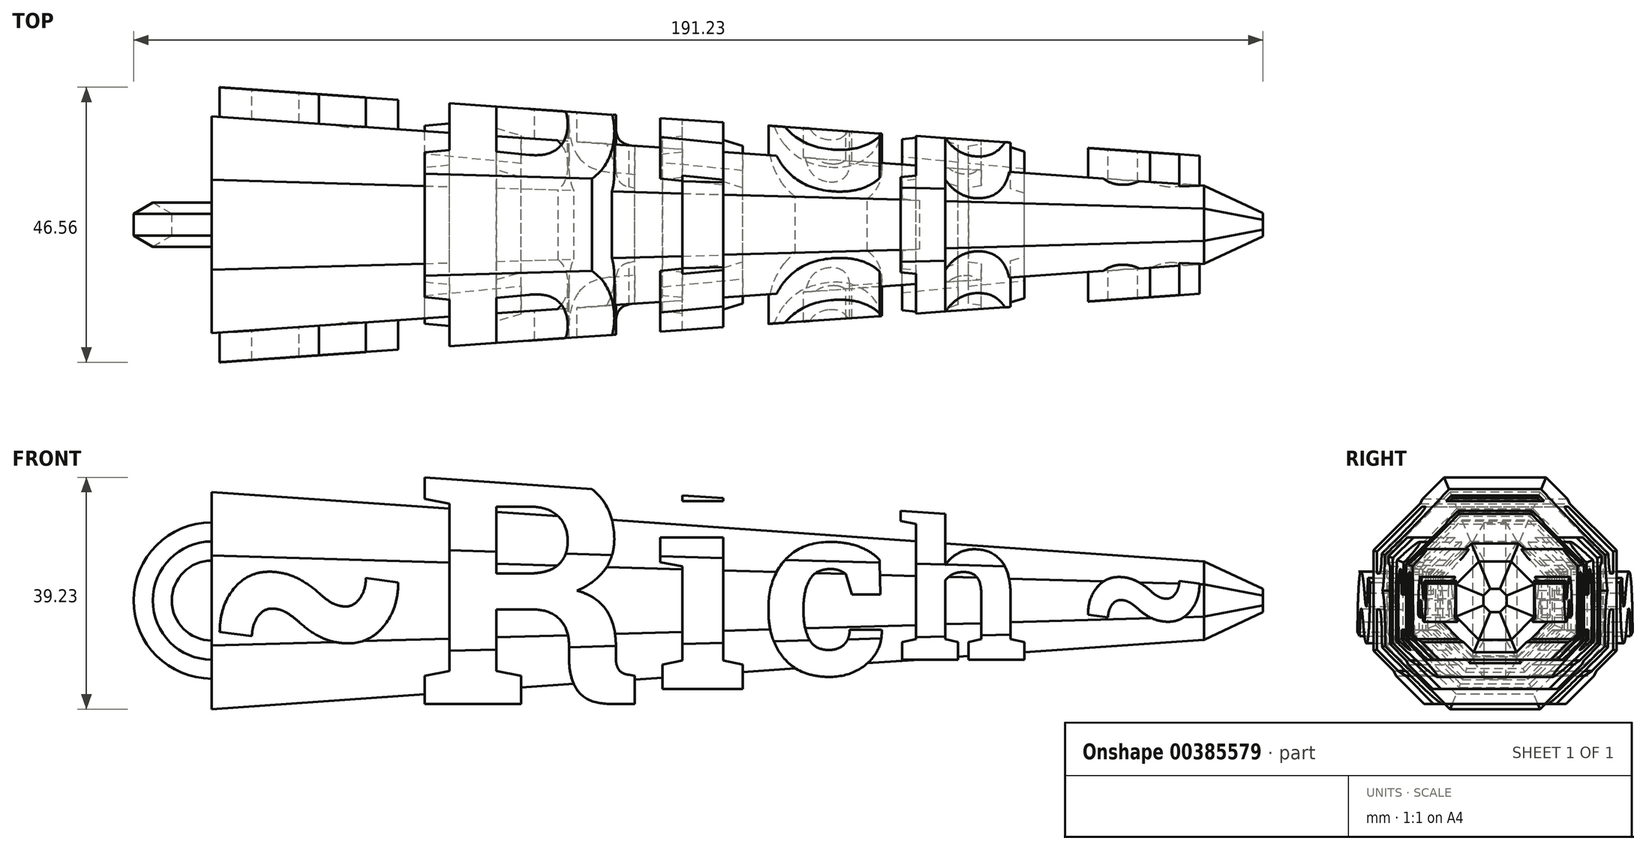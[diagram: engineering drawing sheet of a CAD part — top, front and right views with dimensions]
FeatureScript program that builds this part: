
annotation { "Feature Type Name" : "Feature", "Feature Type Description" : "" }
export const myFeature = defineFeature(function(context is Context, id is Id, definition is map)
    precondition{}
    {
        {
            assignVariable(context, id + "F0", {"name" : "hookPlane", "anyValue" : 84});
        }
        {
            assignVariable(context, id + "F1", {"name" : "halfLength", "anyValue" : 84});
        }
        {
            var Q0;
            Q0=qCreatedBy(makeId("Front.planeOp"),FACE);
            var sketch = newSketch(context, id + "F2", { "sketchPlane" : qUnion([Q0])});
            skText(sketch, "E0", { "text": "~R", "fontName": "RobotoSlab-Bold.ttf"});
            skPoint(sketch, "E1", {"position": v(-8.97, 0) * mm});
            skText(sketch, "E2", { "text": "i", "fontName": "RobotoSlab-Bold.ttf"});
            skText(sketch, "E3", { "text": "c", "fontName": "RobotoSlab-Bold.ttf"});
            skText(sketch, "E4", { "text": "h ~", "fontName": "RobotoSlab-Bold.ttf"});
            skPoint(sketch, "E5", {"position": v(8.89, 0) * mm});
            skPoint(sketch, "E6", {"position": v(32.07, 0) * mm});
            skLineSegment(sketch, "E7", {"start": v(-85.37, -20) * mm, "end": v(-85.37, -51.65) * mm, "construction": true});
            skLineSegment(sketch, "E8", {"start": v(-85.37, -51.65) * mm, "end": v(85.37, -51.65) * mm, "construction": true});
            skLineSegment(sketch, "E9", {"start": v(85.37, -51.65) * mm, "end": v(85.37, -12.5) * mm, "construction": true});
            skPoint(sketch, "E10", {"position": v(0, -51.65) * mm});
            const initialGuessF2  = {"E0": [-0.08537, -0.02, 1, 0, 0.04], "E2": [-0.00897, -0.0175, 1, 0, 0.035], "E3": [0.00889, -0.015, 1, 0, 0.03], "E4": [0.03207, -0.0125, 1, 0, 0.025]};
            skSetInitialGuess(sketch, initialGuessF2);
            skSolve(sketch);
        }
        {
            var Q0;
            Q0=qSketchRegion(id+"F2",true);
            extrude(context, id + "F3", {"entities" : qUnion([Q0]), "depth" : 25 * mm, "hasSecondDirection" : true, "secondDirectionOppositeDirection" : true, "secondDirectionDepth" : 25 * mm});
        }
        {
            var Q0;
            Q0=qCreatedBy(makeId("Right.planeOp"),FACE);
            var sketch = newSketch(context, id + "F4", { "sketchPlane" : qUnion([Q0])});
            skCircle(sketch, "E11", {"center": v(0, -2.5) * mm, "radius": 12.5 * mm, "construction": true});
            skLineSegment(sketch, "E12", {"start": v(0, 19.5) * mm, "end": v(0, 14.75) * mm, "construction": true});
            skLineSegment(sketch, "E13.0", {"start": v(-5.18, 10) * mm, "end": v(5.18, 10) * mm});
            skLineSegment(sketch, "E13.1", {"start": v(5.18, 10) * mm, "end": v(12.5, 2.67) * mm});
            skLineSegment(sketch, "E13.2", {"start": v(12.5, 2.67) * mm, "end": v(12.5, -7.68) * mm});
            skLineSegment(sketch, "E13.3", {"start": v(12.5, -7.68) * mm, "end": v(5.18, -15) * mm});
            skLineSegment(sketch, "E13.4", {"start": v(5.18, -15) * mm, "end": v(-5.18, -15) * mm});
            skLineSegment(sketch, "E13.5", {"start": v(-5.18, -15) * mm, "end": v(-12.5, -7.68) * mm});
            skLineSegment(sketch, "E13.6", {"start": v(-12.5, -7.68) * mm, "end": v(-12.5, 2.67) * mm});
            skLineSegment(sketch, "E13.7", {"start": v(-12.5, 2.67) * mm, "end": v(-5.18, 10) * mm});
            skPoint(sketch, "E13.0.midPoint", {"position": v(0, 10) * mm});
            skLineSegment(sketch, "E14", {"start": v(0, 19.5) * mm, "end": v(0, 10) * mm});
            skSolve(sketch);
        }
        {
            var Q0;
            Q0=qSketchRegion(id+"F4",true);
            var Q1;
            Q1=makeQuery(id+"F3.opExtrude","SWEPT_FACE",FACE,{"disambiguationData":[OSD([sQuery(id+"F2.wireOp",EDGE,"E4.sketch_text.stroke-1")])]});
            extrude(context, id + "F5", {"entities" : qUnion([Q0]), "operationType" : NewBodyOperationType.ADD, "oppositeDirection" : true, "depth" : (getVariable(context, 'halfLength')) * mm, "hasDraft" : true, "draftAngle" : 4 * degree, "hasSecondDirection" : true, "secondDirectionOppositeDirection" : false, "secondDirectionBoundEntityFace" : qUnion([Q1]), "secondDirectionDepth" : (getVariable(context, 'halfLength')) * mm, "hasSecondDirectionDraft" : true, "secondDirectionDraftAngle" : 4 * degree, "secondDirectionDraftPullDirection" : true});
        }
        {
            var Q0;
            Q0=qCreatedBy(makeId("Right.planeOp"),FACE);
            var sketch = newSketch(context, id + "F6", { "sketchPlane" : qUnion([Q0])});
            skCircle(sketch, "E15.cCircle", {"center": v(0, -2.5) * mm, "radius": 17.5 * mm, "construction": true});
            skLineSegment(sketch, "E15.0", {"start": v(-7.25, 15) * mm, "end": v(7.25, 15) * mm});
            skLineSegment(sketch, "E15.1", {"start": v(7.25, 15) * mm, "end": v(17.5, 4.75) * mm});
            skLineSegment(sketch, "E15.2", {"start": v(17.5, 4.75) * mm, "end": v(17.5, -9.75) * mm});
            skLineSegment(sketch, "E15.3", {"start": v(17.5, -9.75) * mm, "end": v(7.25, -20) * mm});
            skLineSegment(sketch, "E15.4", {"start": v(7.25, -20) * mm, "end": v(-7.25, -20) * mm});
            skLineSegment(sketch, "E15.5", {"start": v(-7.25, -20) * mm, "end": v(-17.5, -9.75) * mm});
            skLineSegment(sketch, "E15.6", {"start": v(-17.5, -9.75) * mm, "end": v(-17.5, 4.75) * mm});
            skLineSegment(sketch, "E15.7", {"start": v(-17.5, 4.75) * mm, "end": v(-7.25, 15) * mm});
            skLineSegment(sketch, "E16.bottom", {"start": v(37.5, 35) * mm, "end": v(-37.5, 35) * mm});
            skLineSegment(sketch, "E16.top", {"start": v(37.5, -40) * mm, "end": v(-37.5, -40) * mm});
            skLineSegment(sketch, "E16.left", {"start": v(37.5, 35) * mm, "end": v(37.5, -40) * mm});
            skLineSegment(sketch, "E16.right", {"start": v(-37.5, 35) * mm, "end": v(-37.5, -40) * mm});
            skLineSegment(sketch, "E17", {"start": v(0, 19.5) * mm, "end": v(0, -8.52) * mm, "construction": true});
            skSolve(sketch);
        }
        {
            var Q0;
            Q0=makeQuery(id+"F6.imprint","IMPRINT",FACE,{"disambiguationData":[TD([[makeQuery(id+"F6.imprint","IMPRINT",EDGE,{"derivedFrom":sQuery(id+"F6.wireOp",EDGE,"E15.0")}),1.0]])]});
            extrude(context, id + "F7", {"entities" : qUnion([Q0]), "operationType" : NewBodyOperationType.REMOVE, "endBound" : BoundingType.THROUGH_ALL, "depth" : 25 * mm, "hasDraft" : true, "draftAngle" : 4 * degree, "hasSecondDirection" : true, "secondDirectionBound" : SecondDirectionBoundingType.THROUGH_ALL, "secondDirectionOppositeDirection" : true, "secondDirectionDepth" : 25 * mm, "hasSecondDirectionDraft" : true, "secondDirectionDraftAngle" : 4 * degree, "secondDirectionDraftPullDirection" : true});
        }
        {
            var Q0;
            {var subQ0=sQuery(id+"F4.wireOp",EDGE,"E13.3");var subQ1=sQuery(id+"F4.wireOp",EDGE,"E13.2");var subQ2=sQuery(id+"F4.wireOp",EDGE,"E13.4");var subQ3=sQuery(id+"F4.wireOp",EDGE,"E13.5");var subQ4=sQuery(id+"F4.wireOp",EDGE,"E13.6");Q0=makeQuery(id+"F5.boolean.opBoolean","SPLIT",FACE,{"disambiguationData":[TD([makeQuery(id+"F3.opExtrude","SWEPT_FACE",FACE,{"disambiguationData":[OSD([sQuery(id+"F2.wireOp",EDGE,"E4.sketch_text.stroke-0")])]})])],"derivedFrom":makeQuery(id+"F5.opExtrude","CAP_FACE",FACE,{"disambiguationData":[OSD([sQuery(id+"F4.wireOp",EDGE,"E13.0"),sQuery(id+"F4.wireOp",EDGE,"E13.1"),subQ1,subQ0,subQ2,subQ3,subQ4,sQuery(id+"F4.wireOp",EDGE,"E13.7")])],"isStart":true})});}
            var sketch = newSketch(context, id + "F8", { "sketchPlane" : qUnion([Q0])});
            skCircle(sketch, "E18.cCircle", {"center": v(0, -2.5) * mm, "radius": 6.63 * mm, "construction": true});
            skLineSegment(sketch, "E18.0", {"start": v(-2.74, 4.12) * mm, "end": v(2.74, 4.12) * mm});
            skLineSegment(sketch, "E18.1", {"start": v(2.74, 4.12) * mm, "end": v(6.63, 0.24) * mm});
            skLineSegment(sketch, "E18.2", {"start": v(6.63, 0.24) * mm, "end": v(6.63, -5.25) * mm});
            skLineSegment(sketch, "E18.3", {"start": v(6.63, -5.25) * mm, "end": v(2.74, -9.13) * mm});
            skLineSegment(sketch, "E18.4", {"start": v(2.74, -9.13) * mm, "end": v(-2.74, -9.13) * mm});
            skLineSegment(sketch, "E18.5", {"start": v(-2.74, -9.13) * mm, "end": v(-6.63, -5.25) * mm});
            skLineSegment(sketch, "E18.6", {"start": v(-6.63, -5.25) * mm, "end": v(-6.63, 0.24) * mm});
            skLineSegment(sketch, "E18.7", {"start": v(-6.63, 0.24) * mm, "end": v(-2.74, 4.12) * mm});
            skPoint(sketch, "E18.0.midPoint", {"position": v(0, 4.12) * mm});
            skLineSegment(sketch, "E19", {"start": v(0, 19.59) * mm, "end": v(0, -20.57) * mm, "construction": true});
            skSolve(sketch);
        }
        {
            var Q0;
            Q0=qSketchRegion(id+"F8",true);
            extrude(context, id + "F9", {"entities" : qUnion([Q0]), "operationType" : NewBodyOperationType.ADD, "depth" : 10 * mm, "hasDraft" : true, "draftAngle" : 25 * degree, "draftPullDirection" : true});
        }
        {
            var Q0;
            Q0=qCreatedBy(makeId("Right.planeOp"),FACE);
            cPlane(context, id + "F10", {"entities" : qUnion([Q0]), "cplaneType" : CPlaneType.OFFSET, "offset" : (getVariable(context, 'hookPlane')) * mm, "oppositeDirection" : true, "width" : 150 * mm, "height" : 150 * mm});
        }
        {
            var Q0;
            Q0=qCreatedBy(makeId("Front.planeOp"),FACE);
            var sketch = newSketch(context, id + "F11", { "sketchPlane" : qUnion([Q0])});
            skArc(sketch, "E20", {"start": v(-77.39, 5) * mm, "mid": v(-94, -2.5) * mm, "end": v(-77.39, -10) * mm});
            skLineSegment(sketch, "E21", {"start": v(-77.39, 5) * mm, "end": v(-77.39, -10) * mm, "construction": true});
            skPoint(sketch, "E22", {"position": v(-77.39, -2.5) * mm});
            skLineSegment(sketch, "E23", {"start": v(-84, 15.87) * mm, "end": v(-84, -20.88) * mm, "construction": true});
            skSolve(sketch);
        }
        {
            var Q0;
            Q0=qCreatedBy(id+"F10.planeOp",FACE);
            var sketch = newSketch(context, id + "F12", { "sketchPlane" : qUnion([Q0])});
            skCircle(sketch, "E24.cCircle", {"center": v(0, 7.5) * mm, "radius": 3.23 * mm, "construction": true});
            skLineSegment(sketch, "E24.0", {"start": v(1.87, 4.26) * mm, "end": v(-1.87, 4.26) * mm});
            skLineSegment(sketch, "E24.1", {"start": v(-1.87, 4.26) * mm, "end": v(-3.73, 7.5) * mm});
            skLineSegment(sketch, "E24.2", {"start": v(-3.73, 7.5) * mm, "end": v(-1.87, 10.73) * mm});
            skLineSegment(sketch, "E24.3", {"start": v(-1.87, 10.73) * mm, "end": v(1.87, 10.73) * mm});
            skLineSegment(sketch, "E24.4", {"start": v(1.87, 10.73) * mm, "end": v(3.73, 7.5) * mm});
            skLineSegment(sketch, "E24.5", {"start": v(3.73, 7.5) * mm, "end": v(1.87, 4.26) * mm});
            skPoint(sketch, "E24.0.midPoint", {"position": v(0, 4.26) * mm});
            skSolve(sketch);
        }
        {
            var Q0;
            Q0 = qSketchRegion(id + "F12", true);
            var Q1;
            Q1 = qConstructionFilter(qBodyType(qCreatedBy(id + "F11" ,EDGE), BodyType.WIRE), ConstructionObject.NO);
            sweep(context, id + "F13", {"operationType" : NewBodyOperationType.ADD, "profiles" : qUnion([Q0]), "path" : qUnion([Q1])});
        }
    });
